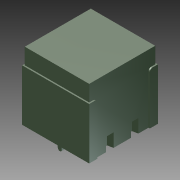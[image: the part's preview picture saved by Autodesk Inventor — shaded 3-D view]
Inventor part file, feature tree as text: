
AUTODESK INVENTOR PART (.ipt)
format: ipt  version: 2011 SP1 (Build 150282100, 282)  size: 167,936 bytes
history: native  units: in
note: dims shown in document units (in); Inventor stores cm internally (conversion verified against a paired STEP export)
features: extrude x8, sketch x8
ambient origin geometry x8: Origin, YZ Plane, XZ Plane, XY Plane, X Axis, Y Axis, Z Axis, Center Point
bodies: Solid1 (feature_tree), body_to_body_c_XY (feature_tree), body_to_body_c_YZ (feature_tree), body_to_body_c_ZX (feature_tree), body_to_body_c_X (feature_tree), body_to_body_c_Y (feature_tree), body_to_body_c_Z (feature_tree), body_to_body_c_Center (feature_tree), body_to_dummy_XY (feature_tree), body_to_dummy_YZ (feature_tree), body_to_dummy_ZX (feature_tree), body_to_dummy_X (feature_tree), body_to_dummy_Y (feature_tree), body_to_dummy_Z (feature_tree), body_to_dummy_Center (feature_tree), body_to_terminal_XY (feature_tree), body_to_terminal_YZ (feature_tree), body_to_terminal_ZX (feature_tree), body_to_terminal_X (feature_tree), body_to_terminal_Y (feature_tree), body_to_terminal_Z (feature_tree), body_to_terminal_Center (feature_tree)
feature tree (16):
  extrude  "Extrusion1"  Depth=0.01in TaperAngle=0.0deg
  extrude  "Extrusion2"  Depth=0.01in TaperAngle=0.0deg
  extrude  "Extrusion3"  Depth=0.1in TaperAngle=0.0deg
  extrude  "Extrusion4"  Depth=0.36in TaperAngle=0.0deg
  extrude  "Extrusion5"  [1 undecoded]
  extrude  "Extrusion6"  [1 undecoded]
  extrude  "Extrusion7"  [1 undecoded]
  extrude  "Extrusion8"  [1 undecoded]
  sketch  "Sketch_1"  dims[d0=0.5in d1=0.0in d2=0.01in d3=0.0in]
  sketch  "Sketch_5"  dims[d4=0.01in d5=0.0in d6=0.01in d7=0.0in]
  sketch  "Sketch_6"  dims[d8=0.01in d9=0.0in d10=0.1in d11=0.0in]
  sketch  "Sketch_7"  dims[d12=0.45in d13=0.0in d14=0.36in d15=0.0in]
  sketch  "Sketch_8"
  sketch  "Sketch_9"
  sketch  "Sketch_10"
  sketch  "Sketch_11"
note: 4 required parameter values undecoded (feature->parameter linkage not recoverable at this tier; creation-order binding heuristic only, values carry confidence <= 0.55)
